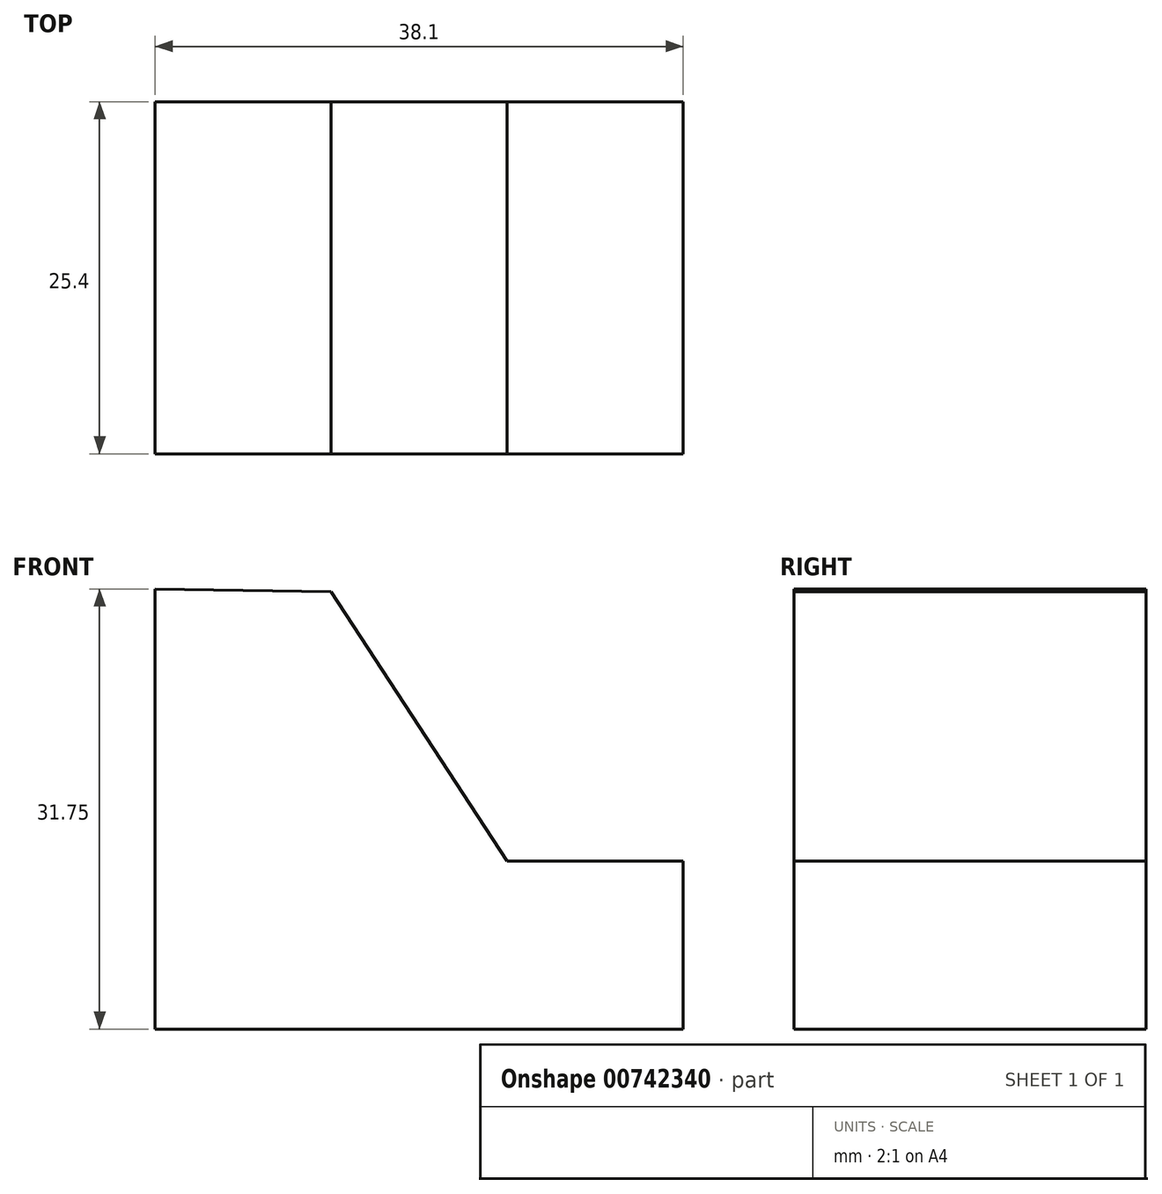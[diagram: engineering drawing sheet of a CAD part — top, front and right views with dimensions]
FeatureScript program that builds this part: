
annotation { "Feature Type Name" : "Feature", "Feature Type Description" : "" }
export const myFeature = defineFeature(function(context is Context, id is Id, definition is map)
    precondition{}
    {
        {
            var Q0;
            Q0=qCreatedBy(makeId("Front.planeOp"),FACE);
            var sketch = newSketch(context, id + "F0", { "sketchPlane" : qUnion([Q0])});
            skLineSegment(sketch, "E0", {"start": v(-38.1, 31.75) * mm, "end": v(-38.1, 0) * mm});
            skLineSegment(sketch, "E1", {"start": v(-38.1, 0) * mm, "end": v(0, 0) * mm});
            skLineSegment(sketch, "E2", {"start": v(0, 0) * mm, "end": v(0, 31.17) * mm});
            skLineSegment(sketch, "E3", {"start": v(0, 31.17) * mm, "end": v(-38.1, 31.75) * mm});
            skSolve(sketch);
        }
        {
            var Q0;
            Q0=makeQuery(id+"F0.imprint","IMPRINT",FACE,{"disambiguationData":[TD([[makeQuery(id+"F0.imprint","IMPRINT",EDGE,{"derivedFrom":sQuery(id+"F0.wireOp",EDGE,"E0")}),1.0]])]});
            extrude(context, id + "F1", {"entities" : qUnion([Q0]), "depth" : 25.4 * mm, "offsetDistance" : 25.4 * mm});
        }
        {
            var Q0;
            Q0=makeQuery(id+"F1.opExtrude","CAP_FACE",FACE,{"disambiguationData":[OSD([sQuery(id+"F0.wireOp",EDGE,"E0"),sQuery(id+"F0.wireOp",EDGE,"E1"),sQuery(id+"F0.wireOp",EDGE,"E2"),sQuery(id+"F0.wireOp",EDGE,"E3")])],"isStart":false});
            var sketch = newSketch(context, id + "F2", { "sketchPlane" : qUnion([Q0])});
            skLineSegment(sketch, "E4", {"start": v(-25.4, 31.56) * mm, "end": v(-12.7, 12.12) * mm});
            skLineSegment(sketch, "E5", {"start": v(-12.7, 12.12) * mm, "end": v(0, 12.12) * mm});
            skLineSegment(sketch, "E6", {"start": v(0, 12.12) * mm, "end": v(0, 31.17) * mm});
            skLineSegment(sketch, "E7", {"start": v(0, 31.17) * mm, "end": v(-25.4, 31.56) * mm});
            skSolve(sketch);
        }
        {
            var Q0;
            Q0=makeQuery(id+"F2.imprint","IMPRINT",FACE,{"disambiguationData":[TD([[makeQuery(id+"F2.imprint","IMPRINT",EDGE,{"derivedFrom":sQuery(id+"F2.wireOp",EDGE,"E4")}),1.0]])]});
            extrude(context, id + "F3", {"entities" : qUnion([Q0]), "operationType" : NewBodyOperationType.REMOVE, "endBound" : BoundingType.THROUGH_ALL, "oppositeDirection" : true, "depth" : 25.4 * mm, "offsetDistance" : 25.4 * mm});
        }
    });
